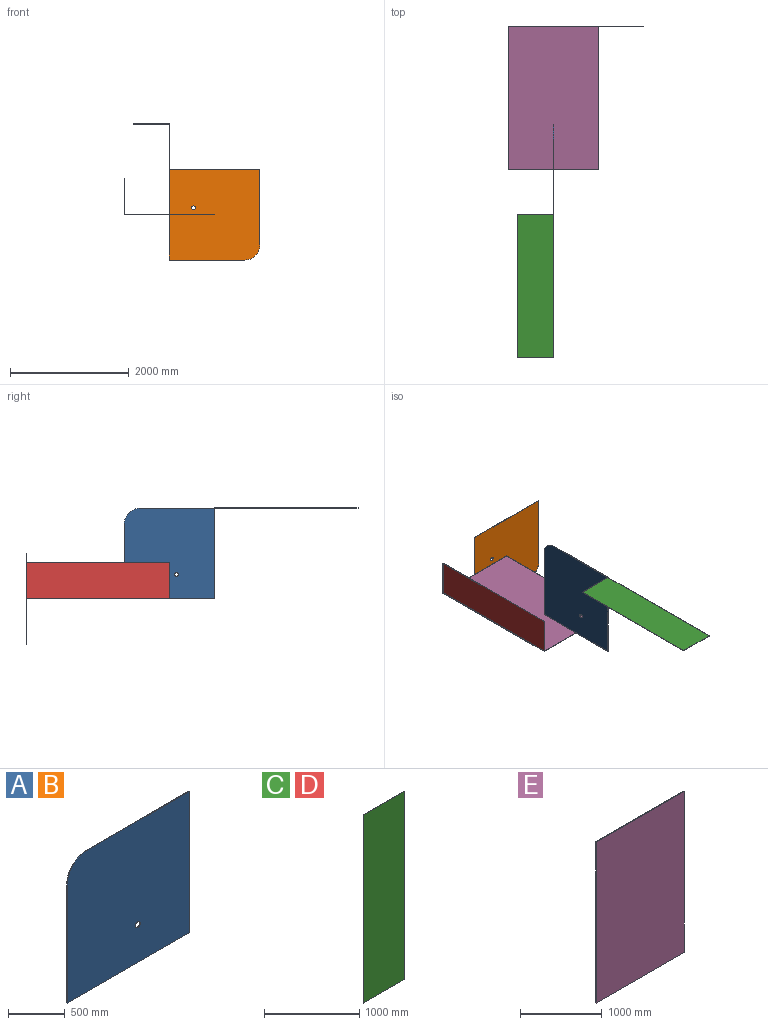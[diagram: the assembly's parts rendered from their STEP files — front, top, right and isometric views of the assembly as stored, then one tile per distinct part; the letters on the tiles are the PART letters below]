
ASSEMBLY  parts=5 mates=4
PART A: 8 faces, bbox 1524x6.4x1524 mm
  f0: plane 1524x6.35mm, normal (1,0,0), area 9677.4mm2, adj f1,f4,f5,f6
  f1: plane 1270x6.35mm, normal (0,0,1), area 8064.5mm2, adj f0,f2,f5,f6
  f2: cylinder r=254mm len=254mm, axis (0,1,0), area 2533.5mm2, adj f1,f3,f5,f6
  f3: plane 1270x6.35mm, normal (-1,0,0), area 8064.5mm2, adj f2,f4,f5,f6
  f4: plane 1524x6.35mm, normal (0,0,-1), area 9677.4mm2, adj f0,f3,f5,f6
  f5: plane 1524x1524mm, normal (0,-1,0), area 2305563.8mm2, adj f0,f1,f2,f3,f4,f7
  f6: plane 1524x1524mm, normal (0,1,0), area 2305563.8mm2, adj f0,f1,f2,f3,f4,f7
  f7: cylinder r=31.75mm len=63.5mm, axis (0,-1,0), area 1266.8mm2, adj f5,f6
PART B: same geometry as A
PART C: 6 faces, bbox 609.6x6.4x2413 mm
  f0: plane 2413x6.35mm, normal (-1,0,0), area 15322.5mm2, adj f1,f3,f4,f5
  f1: plane 609.6x6.35mm, normal (0,0,1), area 3871mm2, adj f0,f2,f4,f5
  f2: plane 2413x6.35mm, normal (1,0,0), area 15322.5mm2, adj f1,f3,f4,f5
  f3: plane 609.6x6.35mm, normal (0,0,-1), area 3871mm2, adj f0,f2,f4,f5
  f4: plane 2413x609.6mm, normal (0,1,0), area 1470964.8mm2, adj f0,f1,f2,f3
  f5: plane 2413x609.6mm, normal (0,-1,0), area 1470964.8mm2, adj f0,f1,f2,f3
PART D: same geometry as C
PART E: 6 faces, bbox 1524x6.4x2413 mm
  f0: plane 2413x6.35mm, normal (-1,0,0), area 15322.5mm2, adj f1,f3,f4,f5
  f1: plane 1524x6.35mm, normal (0,0,1), area 9677.4mm2, adj f0,f2,f4,f5
  f2: plane 2413x6.35mm, normal (1,0,0), area 15322.5mm2, adj f1,f3,f4,f5
  f3: plane 1524x6.35mm, normal (0,0,-1), area 9677.4mm2, adj f0,f2,f4,f5
  f4: plane 2413x1524mm, normal (0,1,0), area 3677412mm2, adj f0,f1,f2,f3
  f5: plane 2413x1524mm, normal (0,-1,0), area 3677412mm2, adj f0,f1,f2,f3
PLACE A rot(axis=(0,0,-1),90deg) t=(1270.73,4165.73,-40.76)mm
PLACE B rot(axis=(0.71,0,0.71),180deg) t=(2026.38,6578.73,-802.76)mm
PLACE C rot(axis=(1,0,0),90deg) t=(1867.63,692.28,1343.54)mm
PLACE D rot(axis=(-0.58,-0.58,-0.58),120deg) t=(1124.68,6874.01,416.44)mm
PLACE E rot(axis=(-1,0,0),90deg) t=(1715.23,5810.38,-809.11)mm
MATE fastened A.f1 <-> C.f5  axis (0,0,1) through (1264.38,3403.73,721.24)mm
MATE fastened E.f5 <-> D.f0  axis (0,0,1) through (502.38,5372.23,-796.41)mm
MATE fastened E.f4 <-> A.f4  axis (0,0,-1) through (1264.38,4165.73,-802.76)mm
MATE fastened E.f1 <-> B.f6  axis (0,1,0) through (1264.38,6578.73,-802.76)mm
